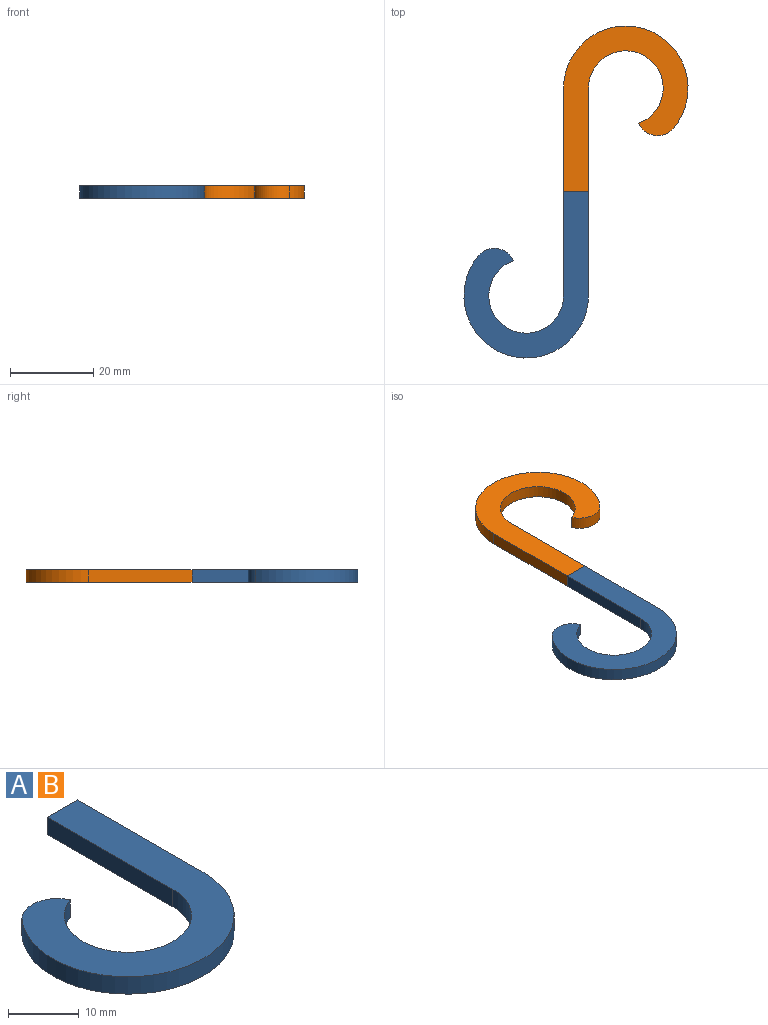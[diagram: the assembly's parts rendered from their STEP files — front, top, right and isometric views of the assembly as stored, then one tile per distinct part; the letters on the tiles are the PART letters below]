
ASSEMBLY  parts=2 mates=1
PART A: 8 faces, bbox 30x40x3 mm
  f0: plane 40x30mm, normal (0,0,1), area 453.2mm2, adj f1,f3,f4,f5,f6,f7
  f1: cylinder r=9mm len=18mm, axis (0,0,1), area 117.8mm2, adj f0,f2,f4,f7
  f2: plane 40x30mm, normal (0,0,-1), area 453.2mm2, adj f1,f3,f4,f5,f6,f7
  f3: cylinder r=15mm len=30mm, axis (0,0,1), area 172.8mm2, adj f0,f2,f5,f7
  f4: plane 25x3mm, normal (-1,0,0), area 75mm2, adj f0,f1,f2,f6
  f5: plane 25x3mm, normal (1,0,0), area 75mm2, adj f0,f2,f3,f6
  f6: plane 6x3mm, normal (0,1,0), area 18mm2, adj f0,f2,f4,f5
  f7: cylinder r=5mm len=8.4mm, axis (0,0,1), area 30.4mm2, adj f0,f1,f2,f3
PART B: same geometry as A
PLACE A t=(26.91,-43.36,-24.43)mm
PLACE B rot(axis=(0,0,-1),180deg) t=(-162.53,6.64,-24.43)mm
MATE fastened A.f6 <-> B.f6  axis (0,1,0) through (-67.81,-18.36,34.69)mm
